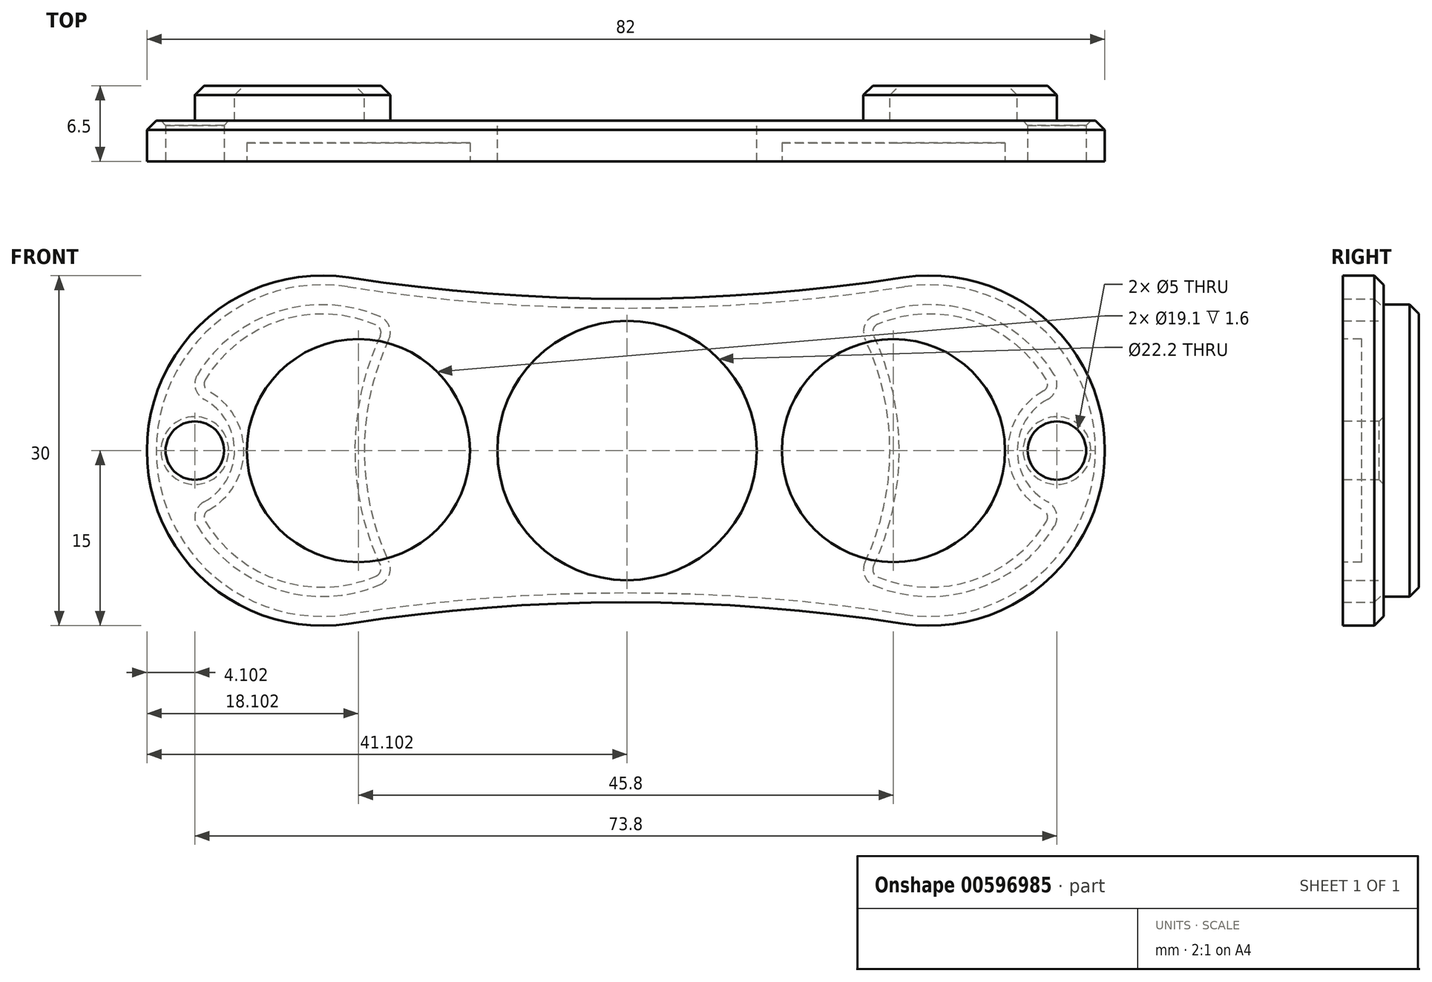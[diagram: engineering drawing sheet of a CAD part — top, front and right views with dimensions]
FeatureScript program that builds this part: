
annotation { "Feature Type Name" : "Feature", "Feature Type Description" : "" }
export const myFeature = defineFeature(function(context is Context, id is Id, definition is map)
    precondition{}
    {
        {
            var Q0;
            Q0=qCreatedBy(makeId("Front.planeOp"),FACE);
            var sketch = newSketch(context, id + "F0", { "sketchPlane" : qUnion([Q0])});
            skCircle(sketch, "E0", {"center": v(-1.84, 0) * mm, "radius": 11.1 * mm});
            skArc(sketch, "E1", {"start": v(-25.64, 14.82) * mm, "mid": v(-42.94, 0) * mm, "end": v(-25.64, -14.82) * mm});
            skArc(sketch, "E2", {"start": v(-25.64, 14.82) * mm, "mid": v(-1.94, 13) * mm, "end": v(21.77, 14.82) * mm});
            skArc(sketch, "E3", {"start": v(21.77, -14.82) * mm, "mid": v(-1.94, -13) * mm, "end": v(-25.64, -14.82) * mm});
            skArc(sketch, "E4.trimOffspring", {"start": v(21.77, -14.82) * mm, "mid": v(39.06, 0) * mm, "end": v(21.77, 14.82) * mm});
            skSolve(sketch);
        }
        {
            var Q0;
            Q0=makeQuery(id+"F0.imprint","IMPRINT",FACE,{"disambiguationData":[TD([[makeQuery(id+"F0.imprint","IMPRINT",EDGE,{"derivedFrom":sQuery(id+"F0.wireOp",EDGE,"E0")}),-1.0]])]});
            extrude(context, id + "F1", {"entities" : qUnion([Q0]), "depth" : 7 * mm, "offsetDistance" : 25 * mm});
        }
        {
            var Q0;
            Q0=makeQuery(id+"F1.opExtrude","CAP_EDGE",EDGE,{"disambiguationData":[OSD([sQuery(id+"F0.wireOp",EDGE,"E1")])],"isStart":false});
            var Q1;
            Q1=makeQuery(id+"F1.opExtrude","CAP_EDGE",EDGE,{"disambiguationData":[OSD([sQuery(id+"F0.wireOp",EDGE,"E3")])],"isStart":false});
            var Q2;
            Q2=makeQuery(id+"F1.opExtrude","CAP_EDGE",EDGE,{"disambiguationData":[OSD([sQuery(id+"F0.wireOp",EDGE,"E3")])],"isStart":true});
            chamfer(context, id + "F2", {"entities" : qUnion([Q0, Q1, Q2]), "width" : .8 * mm, "tangentPropagation" : true});
        }
        {
            var Q0;
            Q0=makeQuery(id+"F1.opExtrude","CAP_FACE",FACE,{"disambiguationData":[OSD([sQuery(id+"F0.wireOp",EDGE,"E0"),sQuery(id+"F0.wireOp",EDGE,"E1"),sQuery(id+"F0.wireOp",EDGE,"E2"),sQuery(id+"F0.wireOp",EDGE,"E3"),sQuery(id+"F0.wireOp",EDGE,"E4.trimOffspring")])],"isStart":false});
            var sketch = newSketch(context, id + "F3", { "sketchPlane" : qUnion([Q0])});
            skCircle(sketch, "E5", {"center": v(-27.94, 0) * mm, "radius": 12.5 * mm});
            skCircle(sketch, "E6", {"center": v(24.06, 0) * mm, "radius": 12.5 * mm});
            skSolve(sketch);
        }
        {
            var Q0;
            Q0=qSketchRegion(id+"F3",true);
            extrude(context, id + "F4", {"entities" : qUnion([Q0]), "operationType" : NewBodyOperationType.ADD, "depth" : 3 * mm, "offsetDistance" : 25 * mm});
        }
        {
            var Q0;
            Q0=makeQuery(id+"F1.opExtrude","CAP_FACE",FACE,{"disambiguationData":[OSD([sQuery(id+"F0.wireOp",EDGE,"E0"),sQuery(id+"F0.wireOp",EDGE,"E1"),sQuery(id+"F0.wireOp",EDGE,"E2"),sQuery(id+"F0.wireOp",EDGE,"E3"),sQuery(id+"F0.wireOp",EDGE,"E4.trimOffspring")])],"isStart":true});
            var sketch = newSketch(context, id + "F5", { "sketchPlane" : qUnion([Q0])});
            skCircle(sketch, "E7", {"center": v(-24.06, 0) * mm, "radius": 12.5 * mm});
            skCircle(sketch, "E8", {"center": v(27.94, 0) * mm, "radius": 12.5 * mm});
            skSolve(sketch);
        }
        {
            var Q0;
            Q0=qSketchRegion(id+"F5",true);
            extrude(context, id + "F6", {"entities" : qUnion([Q0]), "operationType" : NewBodyOperationType.ADD, "depth" : 3 * mm, "offsetDistance" : 25 * mm});
        }
        {
            var Q0;
            Q0=makeQuery(id+"F4.opExtrude","CAP_FACE",FACE,{"disambiguationData":[OSD([sQuery(id+"F3.wireOp",EDGE,"E6")])],"isStart":false});
            var sketch = newSketch(context, id + "F7", { "sketchPlane" : qUnion([Q0])});
            skSolve(sketch);
        }
        {
            var Q0;
            Q0=makeQuery(id+"F4.opExtrude","CAP_FACE",FACE,{"disambiguationData":[OSD([sQuery(id+"F3.wireOp",EDGE,"E5")])],"isStart":false});
            var sketch = newSketch(context, id + "F8", { "sketchPlane" : qUnion([Q0])});
            skCircle(sketch, "E9", {"center": v(-1.84, 0) * mm, "radius": 22.5 * mm});
            skSolve(sketch);
        }
        {
            var Q0;
            Q0=qSketchRegion(id+"F8",true);
            extrude(context, id + "F9", {"entities" : qUnion([Q0]), "operationType" : NewBodyOperationType.REMOVE, "oppositeDirection" : true, "depth" : 3 * mm, "offsetDistance" : 25 * mm});
        }
        {
            var Q0;
            Q0=makeQuery(id+"F6.opExtrude","CAP_FACE",FACE,{"disambiguationData":[OSD([sQuery(id+"F5.wireOp",EDGE,"E7")])],"isStart":false});
            var sketch = newSketch(context, id + "F10", { "sketchPlane" : qUnion([Q0])});
            skCircle(sketch, "E10", {"center": v(1.84, 0) * mm, "radius": 22.5 * mm});
            skSolve(sketch);
        }
        {
            var Q0;
            Q0=qSketchRegion(id+"F10",true);
            extrude(context, id + "F11", {"entities" : qUnion([Q0]), "operationType" : NewBodyOperationType.REMOVE, "oppositeDirection" : true, "depth" : 3 * mm, "offsetDistance" : 25 * mm});
        }
        {
            var Q0;
            Q0=makeQuery(id+"F6.opExtrude","CAP_FACE",FACE,{"disambiguationData":[OSD([sQuery(id+"F5.wireOp",EDGE,"E7")])],"isStart":false});
            var sketch = newSketch(context, id + "F12", { "sketchPlane" : qUnion([Q0])});
            skCircle(sketch, "E11", {"center": v(-36.56, 0) * mm, "radius": 5 * mm});
            skSolve(sketch);
        }
        {
            var Q0;
            Q0=qSketchRegion(id+"F12",true);
            extrude(context, id + "F13", {"entities" : qUnion([Q0]), "operationType" : NewBodyOperationType.REMOVE, "oppositeDirection" : true, "depth" : 3 * mm, "offsetDistance" : 25 * mm});
        }
        {
            var Q0;
            Q0=makeQuery(id+"F6.opExtrude","CAP_FACE",FACE,{"disambiguationData":[OSD([sQuery(id+"F5.wireOp",EDGE,"E8")])],"isStart":false});
            var sketch = newSketch(context, id + "F14", { "sketchPlane" : qUnion([Q0])});
            skCircle(sketch, "E12", {"center": v(40.44, 0) * mm, "radius": 5 * mm});
            skSolve(sketch);
        }
        {
            var Q0;
            Q0=qSketchRegion(id+"F14",true);
            extrude(context, id + "F15", {"entities" : qUnion([Q0]), "operationType" : NewBodyOperationType.REMOVE, "oppositeDirection" : true, "depth" : 3 * mm, "offsetDistance" : 25 * mm});
        }
        {
            var Q0;
            Q0=makeQuery(id+"F4.opExtrude","CAP_FACE",FACE,{"disambiguationData":[OSD([sQuery(id+"F3.wireOp",EDGE,"E5")])],"isStart":false});
            var sketch = newSketch(context, id + "F16", { "sketchPlane" : qUnion([Q0])});
            skCircle(sketch, "E13", {"center": v(-40.44, 0) * mm, "radius": 5 * mm});
            skSolve(sketch);
        }
        {
            var Q0;
            Q0=qSketchRegion(id+"F16",true);
            extrude(context, id + "F17", {"entities" : qUnion([Q0]), "operationType" : NewBodyOperationType.REMOVE, "oppositeDirection" : true, "depth" : 3 * mm, "offsetDistance" : 25 * mm});
        }
        {
            var Q0;
            Q0=makeQuery(id+"F7.imprint","IMPRINT",FACE,{"disambiguationData":[TD([[makeQuery(id+"F7.imprint","IMPRINT",EDGE,{"derivedFrom":makeQuery(id+"F4.opExtrude","CAP_EDGE",EDGE,{"disambiguationData":[OSD([sQuery(id+"F3.wireOp",EDGE,"E6")])],"isStart":false})}),1.0]])]});
            var sketch = newSketch(context, id + "F18", { "sketchPlane" : qUnion([Q0])});
            skCircle(sketch, "E14", {"center": v(36.56, 0) * mm, "radius": 5 * mm});
            skSolve(sketch);
        }
        {
            var Q0;
            Q0=qSketchRegion(id+"F18",true);
            extrude(context, id + "F19", {"entities" : qUnion([Q0]), "operationType" : NewBodyOperationType.REMOVE, "oppositeDirection" : true, "depth" : 3 * mm, "offsetDistance" : 25 * mm});
        }
        {
            var Q0;
            Q0=makeQuery(id+"F17.boolean.opBoolean","INTERSECT",EDGE,{"disambiguationData":[OD(0.0)],"derivedFrom":[makeQuery(id+"F4.opExtrude","SWEPT_FACE",FACE,{"disambiguationData":[OSD([sQuery(id+"F3.wireOp",EDGE,"E5")])]}),makeQuery(id+"F17.opExtrude","SWEPT_FACE",FACE,{"disambiguationData":[OSD([sQuery(id+"F16.wireOp",EDGE,"E13")])]})]});
            var Q1;
            Q1=makeQuery(id+"F17.boolean.opBoolean","INTERSECT",EDGE,{"disambiguationData":[OD(1.0)],"derivedFrom":[makeQuery(id+"F4.opExtrude","SWEPT_FACE",FACE,{"disambiguationData":[OSD([sQuery(id+"F3.wireOp",EDGE,"E5")])]}),makeQuery(id+"F17.opExtrude","SWEPT_FACE",FACE,{"disambiguationData":[OSD([sQuery(id+"F16.wireOp",EDGE,"E13")])]})]});
            var Q2;
            Q2=makeQuery(id+"F9.boolean.opBoolean","INTERSECT",EDGE,{"disambiguationData":[OD(1.0)],"derivedFrom":[makeQuery(id+"F4.opExtrude","SWEPT_FACE",FACE,{"disambiguationData":[OSD([sQuery(id+"F3.wireOp",EDGE,"E5")])]}),makeQuery(id+"F9.opExtrude","SWEPT_FACE",FACE,{"disambiguationData":[OSD([sQuery(id+"F8.wireOp",EDGE,"E9")])]})]});
            var Q3;
            Q3=makeQuery(id+"F9.boolean.opBoolean","INTERSECT",EDGE,{"disambiguationData":[OD(0.0)],"derivedFrom":[makeQuery(id+"F4.opExtrude","SWEPT_FACE",FACE,{"disambiguationData":[OSD([sQuery(id+"F3.wireOp",EDGE,"E5")])]}),makeQuery(id+"F9.opExtrude","SWEPT_FACE",FACE,{"disambiguationData":[OSD([sQuery(id+"F8.wireOp",EDGE,"E9")])]})]});
            var Q4;
            Q4=makeQuery(id+"F9.boolean.opBoolean","INTERSECT",EDGE,{"disambiguationData":[OD(1.0)],"derivedFrom":[makeQuery(id+"F4.opExtrude","SWEPT_FACE",FACE,{"disambiguationData":[OSD([sQuery(id+"F3.wireOp",EDGE,"E6")])]}),makeQuery(id+"F9.opExtrude","SWEPT_FACE",FACE,{"disambiguationData":[OSD([sQuery(id+"F8.wireOp",EDGE,"E9")])]})]});
            var Q5;
            Q5=makeQuery(id+"F9.boolean.opBoolean","INTERSECT",EDGE,{"disambiguationData":[OD(0.0)],"derivedFrom":[makeQuery(id+"F4.opExtrude","SWEPT_FACE",FACE,{"disambiguationData":[OSD([sQuery(id+"F3.wireOp",EDGE,"E6")])]}),makeQuery(id+"F9.opExtrude","SWEPT_FACE",FACE,{"disambiguationData":[OSD([sQuery(id+"F8.wireOp",EDGE,"E9")])]})]});
            var Q6;
            Q6=makeQuery(id+"F19.boolean.opBoolean","INTERSECT",EDGE,{"disambiguationData":[OD(1.0)],"derivedFrom":[makeQuery(id+"F4.opExtrude","SWEPT_FACE",FACE,{"disambiguationData":[OSD([sQuery(id+"F3.wireOp",EDGE,"E6")])]}),makeQuery(id+"F19.opExtrude","SWEPT_FACE",FACE,{"disambiguationData":[OSD([sQuery(id+"F18.wireOp",EDGE,"E14")])]})]});
            var Q7;
            Q7=makeQuery(id+"F19.boolean.opBoolean","INTERSECT",EDGE,{"disambiguationData":[OD(0.0)],"derivedFrom":[makeQuery(id+"F4.opExtrude","SWEPT_FACE",FACE,{"disambiguationData":[OSD([sQuery(id+"F3.wireOp",EDGE,"E6")])]}),makeQuery(id+"F19.opExtrude","SWEPT_FACE",FACE,{"disambiguationData":[OSD([sQuery(id+"F18.wireOp",EDGE,"E14")])]})]});
            var Q8;
            Q8=makeQuery(id+"F11.boolean.opBoolean","INTERSECT",EDGE,{"disambiguationData":[OD(0.0)],"derivedFrom":[makeQuery(id+"F6.opExtrude","SWEPT_FACE",FACE,{"disambiguationData":[OSD([sQuery(id+"F5.wireOp",EDGE,"E8")])]}),makeQuery(id+"F11.opExtrude","SWEPT_FACE",FACE,{"disambiguationData":[OSD([sQuery(id+"F10.wireOp",EDGE,"E10")])]})]});
            var Q9;
            Q9=makeQuery(id+"F11.boolean.opBoolean","INTERSECT",EDGE,{"disambiguationData":[OD(1.0)],"derivedFrom":[makeQuery(id+"F6.opExtrude","SWEPT_FACE",FACE,{"disambiguationData":[OSD([sQuery(id+"F5.wireOp",EDGE,"E8")])]}),makeQuery(id+"F11.opExtrude","SWEPT_FACE",FACE,{"disambiguationData":[OSD([sQuery(id+"F10.wireOp",EDGE,"E10")])]})]});
            var Q10;
            Q10=makeQuery(id+"F15.boolean.opBoolean","INTERSECT",EDGE,{"disambiguationData":[OD(0.0)],"derivedFrom":[makeQuery(id+"F6.opExtrude","SWEPT_FACE",FACE,{"disambiguationData":[OSD([sQuery(id+"F5.wireOp",EDGE,"E8")])]}),makeQuery(id+"F15.opExtrude","SWEPT_FACE",FACE,{"disambiguationData":[OSD([sQuery(id+"F14.wireOp",EDGE,"E12")])]})]});
            var Q11;
            Q11=makeQuery(id+"F15.boolean.opBoolean","INTERSECT",EDGE,{"disambiguationData":[OD(1.0)],"derivedFrom":[makeQuery(id+"F6.opExtrude","SWEPT_FACE",FACE,{"disambiguationData":[OSD([sQuery(id+"F5.wireOp",EDGE,"E8")])]}),makeQuery(id+"F15.opExtrude","SWEPT_FACE",FACE,{"disambiguationData":[OSD([sQuery(id+"F14.wireOp",EDGE,"E12")])]})]});
            var Q12;
            Q12=makeQuery(id+"F11.boolean.opBoolean","INTERSECT",EDGE,{"disambiguationData":[OD(0.0)],"derivedFrom":[makeQuery(id+"F6.opExtrude","SWEPT_FACE",FACE,{"disambiguationData":[OSD([sQuery(id+"F5.wireOp",EDGE,"E7")])]}),makeQuery(id+"F11.opExtrude","SWEPT_FACE",FACE,{"disambiguationData":[OSD([sQuery(id+"F10.wireOp",EDGE,"E10")])]})]});
            var Q13;
            Q13=makeQuery(id+"F11.boolean.opBoolean","INTERSECT",EDGE,{"disambiguationData":[OD(1.0)],"derivedFrom":[makeQuery(id+"F6.opExtrude","SWEPT_FACE",FACE,{"disambiguationData":[OSD([sQuery(id+"F5.wireOp",EDGE,"E7")])]}),makeQuery(id+"F11.opExtrude","SWEPT_FACE",FACE,{"disambiguationData":[OSD([sQuery(id+"F10.wireOp",EDGE,"E10")])]})]});
            var Q14;
            Q14=makeQuery(id+"F13.boolean.opBoolean","INTERSECT",EDGE,{"disambiguationData":[OD(0.0)],"derivedFrom":[makeQuery(id+"F6.opExtrude","SWEPT_FACE",FACE,{"disambiguationData":[OSD([sQuery(id+"F5.wireOp",EDGE,"E7")])]}),makeQuery(id+"F13.opExtrude","SWEPT_FACE",FACE,{"disambiguationData":[OSD([sQuery(id+"F12.wireOp",EDGE,"E11")])]})]});
            var Q15;
            Q15=makeQuery(id+"F13.boolean.opBoolean","INTERSECT",EDGE,{"disambiguationData":[OD(1.0)],"derivedFrom":[makeQuery(id+"F6.opExtrude","SWEPT_FACE",FACE,{"disambiguationData":[OSD([sQuery(id+"F5.wireOp",EDGE,"E7")])]}),makeQuery(id+"F13.opExtrude","SWEPT_FACE",FACE,{"disambiguationData":[OSD([sQuery(id+"F12.wireOp",EDGE,"E11")])]})]});
            fillet(context, id + "F20", {"entities" : qUnion([Q0, Q1, Q2, Q3, Q4, Q5, Q6, Q7, Q8, Q9, Q10, Q11, Q12, Q13, Q14, Q15]), "radius" : 1.5 * mm, "tangentPropagation" : true, "allowEdgeOverflow" : false});
        }
        {
            var Q0;
            Q0=makeQuery(id+"F19.boolean.opBoolean","MERGE",FACE,{"derivedFrom":[makeQuery(id+"F17.boolean.opBoolean","MERGE",FACE,{"derivedFrom":[makeQuery(id+"F9.boolean.opBoolean","MERGE",FACE,{"derivedFrom":[makeQuery(id+"F1.opExtrude","CAP_FACE",FACE,{"disambiguationData":[OSD([sQuery(id+"F0.wireOp",EDGE,"E0"),sQuery(id+"F0.wireOp",EDGE,"E1"),sQuery(id+"F0.wireOp",EDGE,"E2"),sQuery(id+"F0.wireOp",EDGE,"E3"),sQuery(id+"F0.wireOp",EDGE,"E4.trimOffspring")])],"isStart":false}),makeQuery(id+"F9.opExtrude","CAP_FACE",FACE,{"disambiguationData":[OSD([sQuery(id+"F8.wireOp",EDGE,"E9")])],"isStart":false})]}),makeQuery(id+"F17.opExtrude","CAP_FACE",FACE,{"disambiguationData":[OSD([sQuery(id+"F16.wireOp",EDGE,"E13")])],"isStart":false})]}),makeQuery(id+"F19.opExtrude","CAP_FACE",FACE,{"disambiguationData":[OSD([sQuery(id+"F18.wireOp",EDGE,"E14")])],"isStart":false})]});
            var sketch = newSketch(context, id + "F21", { "sketchPlane" : qUnion([Q0])});
            skCircle(sketch, "E15", {"center": v(-38.84, 0) * mm, "radius": 2.5 * mm});
            skSolve(sketch);
        }
        {
            var Q0;
            Q0=qSketchRegion(id+"F21",true);
            extrude(context, id + "F22", {"entities" : qUnion([Q0]), "operationType" : NewBodyOperationType.REMOVE, "oppositeDirection" : true, "depth" : 25 * mm, "offsetDistance" : 25 * mm});
        }
        {
            var Q0;
            Q0=makeQuery(id+"F19.boolean.opBoolean","MERGE",FACE,{"derivedFrom":[makeQuery(id+"F17.boolean.opBoolean","MERGE",FACE,{"derivedFrom":[makeQuery(id+"F9.boolean.opBoolean","MERGE",FACE,{"derivedFrom":[makeQuery(id+"F1.opExtrude","CAP_FACE",FACE,{"disambiguationData":[OSD([sQuery(id+"F0.wireOp",EDGE,"E0"),sQuery(id+"F0.wireOp",EDGE,"E1"),sQuery(id+"F0.wireOp",EDGE,"E2"),sQuery(id+"F0.wireOp",EDGE,"E3"),sQuery(id+"F0.wireOp",EDGE,"E4.trimOffspring")])],"isStart":false}),makeQuery(id+"F9.opExtrude","CAP_FACE",FACE,{"disambiguationData":[OSD([sQuery(id+"F8.wireOp",EDGE,"E9")])],"isStart":false})]}),makeQuery(id+"F17.opExtrude","CAP_FACE",FACE,{"disambiguationData":[OSD([sQuery(id+"F16.wireOp",EDGE,"E13")])],"isStart":false})]}),makeQuery(id+"F19.opExtrude","CAP_FACE",FACE,{"disambiguationData":[OSD([sQuery(id+"F18.wireOp",EDGE,"E14")])],"isStart":false})]});
            var sketch = newSketch(context, id + "F23", { "sketchPlane" : qUnion([Q0])});
            skCircle(sketch, "E16", {"center": v(34.96, 0) * mm, "radius": 2.5 * mm});
            skSolve(sketch);
        }
        {
            var Q0;
            Q0=qSketchRegion(id+"F23",true);
            extrude(context, id + "F24", {"entities" : qUnion([Q0]), "operationType" : NewBodyOperationType.REMOVE, "oppositeDirection" : true, "depth" : 25 * mm, "offsetDistance" : 25 * mm});
        }
        {
            var Q0;
            Q0=makeQuery(id+"F22.boolean.opBoolean","COPY",EDGE,{"derivedFrom":makeQuery(id+"F22.opExtrude","CAP_EDGE",EDGE,{"disambiguationData":[OSD([sQuery(id+"F21.wireOp",EDGE,"E15")])],"isStart":true})});
            var Q1;
            Q1=makeQuery(id+"F24.boolean.opBoolean","COPY",EDGE,{"derivedFrom":makeQuery(id+"F24.opExtrude","CAP_EDGE",EDGE,{"disambiguationData":[OSD([sQuery(id+"F23.wireOp",EDGE,"E16")])],"isStart":true})});
            var Q2;
            Q2=makeQuery(id+"F24.boolean.opBoolean","INTERSECT",EDGE,{"derivedFrom":[makeQuery(id+"F15.boolean.opBoolean","MERGE",FACE,{"derivedFrom":[makeQuery(id+"F13.boolean.opBoolean","MERGE",FACE,{"derivedFrom":[makeQuery(id+"F11.boolean.opBoolean","MERGE",FACE,{"derivedFrom":[makeQuery(id+"F1.opExtrude","CAP_FACE",FACE,{"disambiguationData":[OSD([sQuery(id+"F0.wireOp",EDGE,"E0"),sQuery(id+"F0.wireOp",EDGE,"E1"),sQuery(id+"F0.wireOp",EDGE,"E2"),sQuery(id+"F0.wireOp",EDGE,"E3"),sQuery(id+"F0.wireOp",EDGE,"E4.trimOffspring")])],"isStart":true}),makeQuery(id+"F11.opExtrude","CAP_FACE",FACE,{"disambiguationData":[OSD([sQuery(id+"F10.wireOp",EDGE,"E10")])],"isStart":false})]}),makeQuery(id+"F13.opExtrude","CAP_FACE",FACE,{"disambiguationData":[OSD([sQuery(id+"F12.wireOp",EDGE,"E11")])],"isStart":false})]}),makeQuery(id+"F15.opExtrude","CAP_FACE",FACE,{"disambiguationData":[OSD([sQuery(id+"F14.wireOp",EDGE,"E12")])],"isStart":false})]}),makeQuery(id+"F24.opExtrude","SWEPT_FACE",FACE,{"disambiguationData":[OSD([sQuery(id+"F23.wireOp",EDGE,"E16")])]})]});
            var Q3;
            Q3=makeQuery(id+"F22.boolean.opBoolean","INTERSECT",EDGE,{"derivedFrom":[makeQuery(id+"F15.boolean.opBoolean","MERGE",FACE,{"derivedFrom":[makeQuery(id+"F13.boolean.opBoolean","MERGE",FACE,{"derivedFrom":[makeQuery(id+"F11.boolean.opBoolean","MERGE",FACE,{"derivedFrom":[makeQuery(id+"F1.opExtrude","CAP_FACE",FACE,{"disambiguationData":[OSD([sQuery(id+"F0.wireOp",EDGE,"E0"),sQuery(id+"F0.wireOp",EDGE,"E1"),sQuery(id+"F0.wireOp",EDGE,"E2"),sQuery(id+"F0.wireOp",EDGE,"E3"),sQuery(id+"F0.wireOp",EDGE,"E4.trimOffspring")])],"isStart":true}),makeQuery(id+"F11.opExtrude","CAP_FACE",FACE,{"disambiguationData":[OSD([sQuery(id+"F10.wireOp",EDGE,"E10")])],"isStart":false})]}),makeQuery(id+"F13.opExtrude","CAP_FACE",FACE,{"disambiguationData":[OSD([sQuery(id+"F12.wireOp",EDGE,"E11")])],"isStart":false})]}),makeQuery(id+"F15.opExtrude","CAP_FACE",FACE,{"disambiguationData":[OSD([sQuery(id+"F14.wireOp",EDGE,"E12")])],"isStart":false})]}),makeQuery(id+"F22.opExtrude","SWEPT_FACE",FACE,{"disambiguationData":[OSD([sQuery(id+"F21.wireOp",EDGE,"E15")])]})]});
            chamfer(context, id + "F25", {"entities" : qUnion([Q0, Q1, Q2, Q3]), "width" : 0.4 * mm, "tangentPropagation" : true});
        }
        {
            var Q0;
            Q0=makeQuery(id+"F4.opExtrude","CAP_FACE",FACE,{"disambiguationData":[OSD([sQuery(id+"F3.wireOp",EDGE,"E6")])],"isStart":false});
            var Q1;
            Q1=makeQuery(id+"F4.opExtrude","CAP_FACE",FACE,{"disambiguationData":[OSD([sQuery(id+"F3.wireOp",EDGE,"E5")])],"isStart":false});
            var Q2;
            Q2=makeQuery(id+"F6.opExtrude","CAP_FACE",FACE,{"disambiguationData":[OSD([sQuery(id+"F5.wireOp",EDGE,"E8")])],"isStart":false});
            var Q3;
            Q3=makeQuery(id+"F6.opExtrude","CAP_FACE",FACE,{"disambiguationData":[OSD([sQuery(id+"F5.wireOp",EDGE,"E7")])],"isStart":false});
            chamfer(context, id + "F26", {"entities" : qUnion([Q0, Q1, Q2, Q3]), "width" : .8 * mm, "tangentPropagation" : true});
        }
        {
            var Q0;
            Q0=makeQuery(id+"F4.opExtrude","CAP_FACE",FACE,{"disambiguationData":[OSD([sQuery(id+"F3.wireOp",EDGE,"E5")])],"isStart":false});
            var sketch = newSketch(context, id + "F27", { "sketchPlane" : qUnion([Q0])});
            skLineSegment(sketch, "E17.bottom", {"start": v(-54.9, 24.67) * mm, "end": v(48.36, 24.67) * mm});
            skLineSegment(sketch, "E17.top", {"start": v(-54.9, -24.67) * mm, "end": v(48.36, -24.67) * mm});
            skLineSegment(sketch, "E17.left", {"start": v(-54.9, 24.67) * mm, "end": v(-54.9, -24.67) * mm});
            skLineSegment(sketch, "E17.right", {"start": v(48.36, 24.67) * mm, "end": v(48.36, -24.67) * mm});
            skSolve(sketch);
        }
        {
            var Q0;
            Q0=qSketchRegion(id+"F27",true);
            extrude(context, id + "F28", {"entities" : qUnion([Q0]), "operationType" : NewBodyOperationType.REMOVE, "oppositeDirection" : true, "depth" : 6.5 * mm, "offsetDistance" : 25 * mm});
        }
        {
            var Q0;
            Q0=makeQuery(id+"F28.boolean.opBoolean","COPY",FACE,{"derivedFrom":makeQuery(id+"F28.opExtrude","CAP_FACE",FACE,{"disambiguationData":[OSD([sQuery(id+"F27.wireOp",EDGE,"E17.bottom"),sQuery(id+"F27.wireOp",EDGE,"E17.top"),sQuery(id+"F27.wireOp",EDGE,"E17.left"),sQuery(id+"F27.wireOp",EDGE,"E17.right")])],"isStart":false})});
            var sketch = newSketch(context, id + "F29", { "sketchPlane" : qUnion([Q0])});
            skCircle(sketch, "E18", {"center": v(-24.84, 0) * mm, "radius": 9.55 * mm});
            skCircle(sketch, "E19", {"center": v(20.96, 0) * mm, "radius": 9.55 * mm});
            skSolve(sketch);
        }
        {
            var Q0;
            Q0=makeQuery(id+"F29.imprint","IMPRINT",FACE,{"disambiguationData":[TD([[makeQuery(id+"F29.imprint","IMPRINT",EDGE,{"derivedFrom":sQuery(id+"F29.wireOp",EDGE,"E18")}),1.0]])]});
            var Q1;
            Q1=makeQuery(id+"F29.imprint","IMPRINT",FACE,{"disambiguationData":[TD([[makeQuery(id+"F29.imprint","IMPRINT",EDGE,{"derivedFrom":sQuery(id+"F29.wireOp",EDGE,"E19")}),1.0]])]});
            extrude(context, id + "F30", {"entities" : qUnion([Q0, Q1]), "operationType" : NewBodyOperationType.REMOVE, "oppositeDirection" : true, "depth" : 1.6 * mm, "offsetDistance" : 25 * mm});
        }
    });
